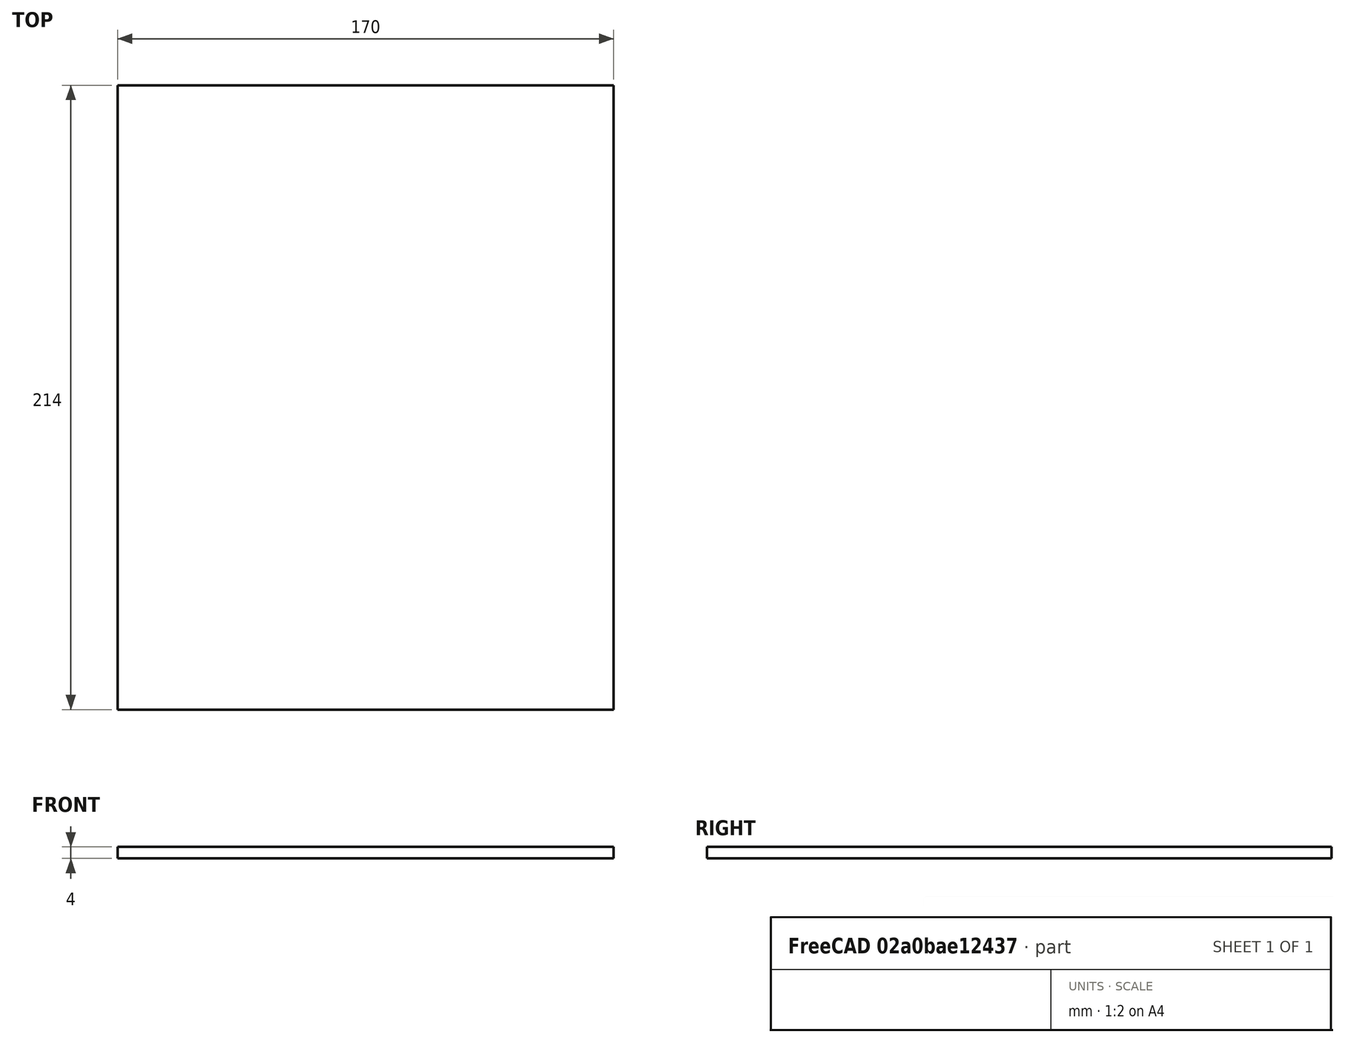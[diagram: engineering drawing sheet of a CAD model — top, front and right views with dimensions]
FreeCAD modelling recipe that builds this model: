
FCSTD DOCUMENT  (FreeCAD 0.17R13528 (Git))
Label: Mirror
License: All rights reserved
LicenseURL: http://en.wikipedia.org/wiki/All_rights_reserved
objects: Sketcher::SketchObject×1, PartDesign::Pad×1, PartDesign::Body×1
note: 4 computed .brp shape members not serialized (recipe doc carries the construction recipe); baked Part::Feature solids carry a one-line shape summary decoded from their .brp

FEATURE [Sketcher::SketchObject] Sketch
  MapMode = 5
  Support = -> [XY_Plane]
  sketch-geometry (4):
    g0: LineSegment StartX=0 StartY=0 StartZ=0 EndX=170 EndY=0 EndZ=0
    g1: LineSegment StartX=170 StartY=0 StartZ=0 EndX=170 EndY=214 EndZ=0
    g2: LineSegment StartX=170 StartY=214 StartZ=0 EndX=0 EndY=214 EndZ=0
    g3: LineSegment StartX=0 StartY=214 StartZ=0 EndX=0 EndY=0 EndZ=0
  constraints (11):
    c: Coincident(g0,g1)
    c: Coincident(g1,g2)
    c: Coincident(g2,g3)
    c: Coincident(g3,g0)
    c: Horizontal(g0)
    c: Horizontal(g2)
    c: Vertical(g1)
    c: Vertical(g3)
    c: Coincident(g0,g-1)
    c: DistanceX(g0,g0) = 170
    c: DistanceY(g3,g3) = 214
FEATURE [PartDesign::Pad] Pad
  Length = 4
  Length2 = 100
  Profile = -> Sketch
  Type = 0
  expr: Length = Data#Spreadsheet.B1
FEATURE [PartDesign::Body] Body
  Group = -> [Sketch,Pad]
  Origin = -> Origin
  Tip = -> Pad
